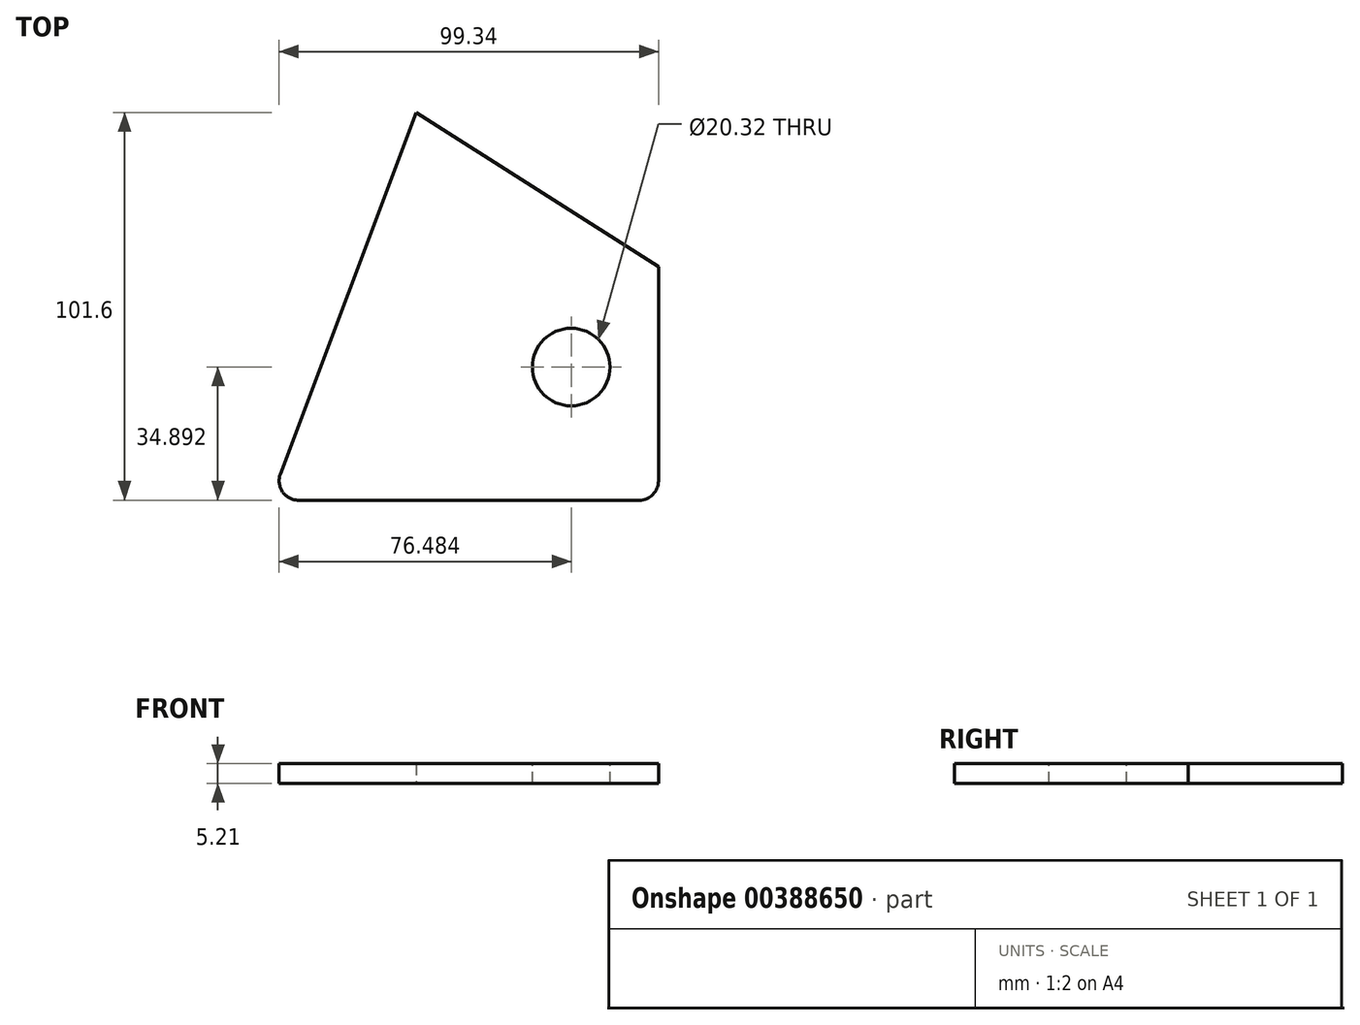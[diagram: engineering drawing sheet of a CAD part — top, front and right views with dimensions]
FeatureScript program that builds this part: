
annotation { "Feature Type Name" : "Feature", "Feature Type Description" : "" }
export const myFeature = defineFeature(function(context is Context, id is Id, definition is map)
    precondition{}
    {
        {
            var Q0;
            Q0=qCreatedBy(makeId("Top.planeOp"),FACE);
            var sketch = newSketch(context, id + "F0", { "sketchPlane" : qUnion([Q0])});
            skLineSegment(sketch, "E0.bottom", {"start": v(56.82, -50.8) * mm, "end": v(-44.78, -50.8) * mm});
            skLineSegment(sketch, "E0.top", {"start": v(56.82, 50.8) * mm, "end": v(-44.78, 50.8) * mm});
            skLineSegment(sketch, "E0.left", {"start": v(56.82, -50.8) * mm, "end": v(56.82, 50.8) * mm});
            skLineSegment(sketch, "E0.right", {"start": v(-44.78, -50.8) * mm, "end": v(-44.78, 50.8) * mm});
            skPoint(sketch, "E0.middle", {"position": v(6.02, 0) * mm});
            skLineSegment(sketch, "E1", {"start": v(-44.78, -50.8) * mm, "end": v(-6.65, 50.8) * mm});
            skLineSegment(sketch, "E2", {"start": v(-6.65, 50.8) * mm, "end": v(56.82, 10.4) * mm});
            skSolve(sketch);
        }
        {
            var Q0;
            {var subQ0=sQuery(id+"F0.wireOp",EDGE,"E0.bottom");Q0=makeQuery(id+"F0.imprint","IMPRINT",FACE,{"disambiguationData":[TD([[makeQuery(id+"F0.imprint","IMPRINT",EDGE,{"derivedFrom":subQ0}),-1.0]])]});}
            extrude(context, id + "F1", {"entities" : qUnion([Q0]), "depth" : 5.2 * mm});
        }
        {
            var Q0;
            Q0=makeQuery(id+"F1.opExtrude","CAP_FACE",FACE,{"disambiguationData":[OSD([sQuery(id+"F0.wireOp",EDGE,"E0.bottom"),sQuery(id+"F0.wireOp",EDGE,"E0.left"),sQuery(id+"F0.wireOp",EDGE,"E1"),sQuery(id+"F0.wireOp",EDGE,"E2")])],"isStart":false});
            var sketch = newSketch(context, id + "F2", { "sketchPlane" : qUnion([Q0])});
            skCircle(sketch, "E3", {"center": v(33.96, -15.9) * mm, "radius": 10.16 * mm});
            skSolve(sketch);
        }
        {
            var Q0;
            Q0 = qSketchRegion(id + "F2", true);
            extrude(context, id + "F3", {"entities" : qUnion([Q0]), "operationType" : NewBodyOperationType.REMOVE, "endBound" : BoundingType.UP_TO_NEXT, "oppositeDirection" : true, "depth" : 25.4 * mm});
        }
        {
            var Q0;
            Q0=makeQuery(id+"F1.opExtrude","SWEPT_EDGE",EDGE,{"disambiguationData":[OSD([sQuery(id+"F0.wireOp",EDGE,"E0.bottom"),sQuery(id+"F0.wireOp",EDGE,"E0.left")])]});
            var Q1;
            Q1=makeQuery(id+"F1.opExtrude","SWEPT_EDGE",EDGE,{"disambiguationData":[OSD([sQuery(id+"F0.wireOp",EDGE,"E0.bottom"),sQuery(id+"F0.wireOp",EDGE,"E0.right"),sQuery(id+"F0.wireOp",EDGE,"E1")])]});
            fillet(context, id + "F4", {"entities" : qUnion([Q0, Q1]), "radius" : 5.08 * mm, "tangentPropagation" : true, "allowEdgeOverflow" : false});
        }
    });
